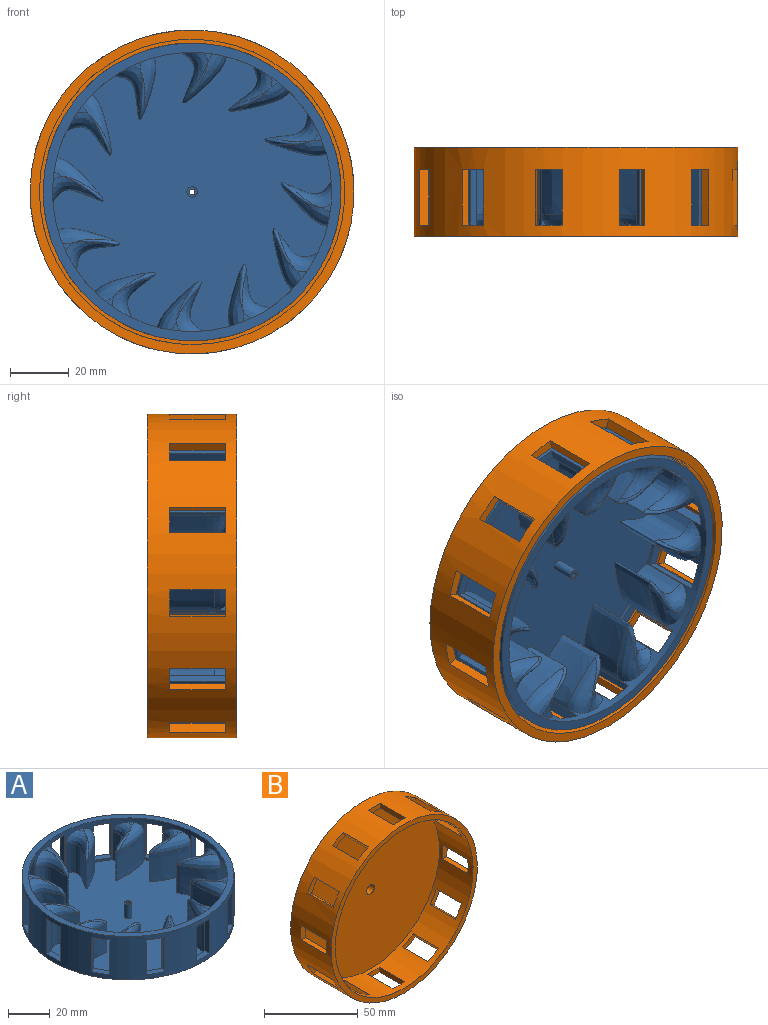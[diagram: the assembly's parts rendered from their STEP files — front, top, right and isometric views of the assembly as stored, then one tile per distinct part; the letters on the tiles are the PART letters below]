
ASSEMBLY  parts=2 mates=1
PART A: 116 faces, bbox 102.8x102.5x25.4 mm
  f0: plane 95.27x95.27mm, normal (0,0,1), area 5619.9mm2, adj f2,f54,f56,f58,f60,f62,f64,f66
  f1: cylinder r=50.8mm len=101.6mm, axis (0,0,-1), area 5873.4mm2, adj f3,f4,f5,f6,f7,f8,f9,f10
  f2: cylinder r=47.64mm len=95.27mm, axis (0,0,-1), area 1163.8mm2, adj f0,f4,f5,f6,f7,f8,f9,f10
  f3: plane 101.6x101.6mm, normal (0,0,-1), area 8104.2mm2, adj f1,f53
  f4: plane 101.6x101.6mm, normal (0,0,1), area 978.6mm2, adj f1,f2
  f5: plane 20.32x3.18mm, normal (1,0,0), area 64.6mm2, adj f1,f2,f6,f7
  f6: plane 9.15x3.39mm, normal (0,0,1), area 29mm2, adj f1,f2,f5,f8
  f7: plane 9.15x3.39mm, normal (0,0,-1), area 29mm2, adj f1,f2,f5,f8
  f8: plane 20.32x3.18mm, normal (-1,0,0), area 64.6mm2, adj f1,f2,f6,f7
  f9: plane 9.51x7.33mm, normal (0,0,1), area 29mm2, adj f1,f2,f11,f12
  f10: plane 9.51x7.33mm, normal (0,0,-1), area 29mm2, adj f1,f2,f11,f12
  f11: plane 20.32x2.75mm, normal (0.87,0.5,0), area 64.6mm2, adj f1,f2,f9,f10
  f12: plane 20.32x2.75mm, normal (-0.87,-0.5,0), area 64.6mm2, adj f1,f2,f9,f10
  f13: plane 9.51x7.32mm, normal (0,0,1), area 29mm2, adj f1,f2,f14,f16
  f14: plane 20.32x2.75mm, normal (-0.5,-0.87,0), area 64.6mm2, adj f1,f2,f13,f15
  f15: plane 9.51x7.32mm, normal (0,0,-1), area 29mm2, adj f1,f2,f14,f16
  f16: plane 20.32x2.75mm, normal (0.5,0.87,0), area 64.6mm2, adj f1,f2,f13,f15
  f17: plane 20.32x3.18mm, normal (0,1,0), area 64.6mm2, adj f1,f2,f18,f19
  f18: plane 9.15x3.39mm, normal (0,0,1), area 29mm2, adj f1,f2,f17,f20
  f19: plane 9.15x3.39mm, normal (0,0,-1), area 29mm2, adj f1,f2,f17,f20
  f20: plane 20.32x3.18mm, normal (0,-1,0), area 64.6mm2, adj f1,f2,f18,f19
  f21: plane 9.51x7.33mm, normal (0,0,1), area 29mm2, adj f1,f2,f23,f24
  f22: plane 9.51x7.33mm, normal (0,0,-1), area 29mm2, adj f1,f2,f23,f24
  f23: plane 20.32x2.75mm, normal (-0.5,0.87,0), area 64.6mm2, adj f1,f2,f21,f22
  f24: plane 20.32x2.75mm, normal (0.5,-0.87,0), area 64.6mm2, adj f1,f2,f21,f22
  f25: plane 9.51x7.32mm, normal (0,0,1), area 29mm2, adj f1,f2,f26,f28
  f26: plane 20.32x2.75mm, normal (0.87,-0.5,0), area 64.6mm2, adj f1,f2,f25,f27
  f27: plane 9.51x7.32mm, normal (0,0,-1), area 29mm2, adj f1,f2,f26,f28
  f28: plane 20.32x2.75mm, normal (-0.87,0.5,0), area 64.6mm2, adj f1,f2,f25,f27
  f29: plane 20.32x3.18mm, normal (-1,0,0), area 64.6mm2, adj f1,f2,f30,f31
  f30: plane 9.15x3.39mm, normal (0,0,1), area 29mm2, adj f1,f2,f29,f32
  f31: plane 9.15x3.39mm, normal (0,0,-1), area 29mm2, adj f1,f2,f29,f32
  f32: plane 20.32x3.18mm, normal (1,0,0), area 64.6mm2, adj f1,f2,f30,f31
  f33: plane 9.51x7.33mm, normal (0,0,1), area 29mm2, adj f1,f2,f35,f36
  f34: plane 9.51x7.33mm, normal (0,0,-1), area 29mm2, adj f1,f2,f35,f36
  f35: plane 20.32x2.75mm, normal (-0.87,-0.5,0), area 64.6mm2, adj f1,f2,f33,f34
  f36: plane 20.32x2.75mm, normal (0.87,0.5,0), area 64.6mm2, adj f1,f2,f33,f34
  f37: plane 9.51x7.32mm, normal (0,0,1), area 29mm2, adj f1,f2,f38,f40
  f38: plane 20.32x2.75mm, normal (0.5,0.87,0), area 64.6mm2, adj f1,f2,f37,f39
  f39: plane 9.51x7.32mm, normal (0,0,-1), area 29mm2, adj f1,f2,f38,f40
  f40: plane 20.32x2.75mm, normal (-0.5,-0.87,0), area 64.6mm2, adj f1,f2,f37,f39
  f41: plane 20.32x3.18mm, normal (0,-1,0), area 64.6mm2, adj f1,f2,f42,f43
  f42: plane 9.15x3.39mm, normal (0,0,1), area 29mm2, adj f1,f2,f41,f44
  f43: plane 9.15x3.39mm, normal (0,0,-1), area 29mm2, adj f1,f2,f41,f44
  f44: plane 20.32x3.18mm, normal (0,1,0), area 64.6mm2, adj f1,f2,f42,f43
  f45: plane 9.51x7.33mm, normal (0,0,1), area 29mm2, adj f1,f2,f47,f48
  f46: plane 9.51x7.33mm, normal (0,0,-1), area 29mm2, adj f1,f2,f47,f48
  f47: plane 20.32x2.75mm, normal (0.5,-0.87,0), area 64.6mm2, adj f1,f2,f45,f46
  f48: plane 20.32x2.75mm, normal (-0.5,0.87,0), area 64.6mm2, adj f1,f2,f45,f46
  f49: plane 9.51x7.32mm, normal (0,0,1), area 29mm2, adj f1,f2,f50,f52
  f50: plane 20.32x2.75mm, normal (-0.87,0.5,0), area 64.6mm2, adj f1,f2,f49,f51
  f51: plane 9.51x7.32mm, normal (0,0,-1), area 29mm2, adj f1,f2,f50,f52
  f52: plane 20.32x2.75mm, normal (0.87,-0.5,0), area 64.6mm2, adj f1,f2,f49,f51
  f53: cylinder r=0.99mm len=9.25mm, axis (0,0,1), area 57.5mm2, adj f3,f115
  f54: extruded ~21.39x16.51mm, area 688.7mm2, adj f0,f2,f78,f79,f80
  f55: plane 3.32x2.87mm, normal (0,0,1), area 4.2mm2, adj f2,f78,f80
  f56: extruded ~19.84x16.51mm, area 693.4mm2, adj f0,f2,f111,f112,f113
  f57: plane 2.98x2.71mm, normal (0,0,1), area 3.9mm2, adj f2,f111,f113
  f58: extruded ~17.34x16.94mm, area 693.4mm2, adj f0,f2,f108,f109,f110
  f59: plane 3.19x2.64mm, normal (0,0,1), area 3.9mm2, adj f2,f108,f110
  f60: extruded ~21.41x16.51mm, area 693.4mm2, adj f0,f2,f105,f106,f107
  f61: plane 3.19x2.75mm, normal (0,0,1), area 3.9mm2, adj f2,f105,f107
  f62: extruded ~19.84x16.51mm, area 693.4mm2, adj f0,f2,f102,f103,f104
  f63: plane 2.98x2.71mm, normal (0,0,1), area 3.9mm2, adj f2,f102,f104
  f64: extruded ~17.34x16.94mm, area 693.4mm2, adj f0,f2,f81,f82,f83
  f65: plane 3.19x2.64mm, normal (0,0,1), area 3.9mm2, adj f2,f81,f83
  f66: extruded ~19.84x16.51mm, area 693.4mm2, adj f0,f2,f84,f85,f86
  f67: plane 2.98x2.71mm, normal (0,0,1), area 3.9mm2, adj f2,f84,f86
  f68: extruded ~21.41x16.51mm, area 693.4mm2, adj f0,f2,f87,f88,f89
  f69: plane 3.19x2.75mm, normal (0,0,1), area 3.9mm2, adj f2,f87,f89
  f70: extruded ~17.34x16.94mm, area 693.4mm2, adj f0,f2,f90,f91,f92
  f71: plane 3.19x2.64mm, normal (0,0,1), area 3.9mm2, adj f2,f90,f92
  f72: extruded ~19.84x16.51mm, area 693.4mm2, adj f0,f2,f93,f94,f95
  f73: plane 2.98x2.71mm, normal (0,0,1), area 3.9mm2, adj f2,f93,f95
  f74: extruded ~21.41x16.51mm, area 693.4mm2, adj f0,f2,f96,f97,f98
  f75: plane 3.19x2.75mm, normal (0,0,1), area 3.9mm2, adj f2,f96,f98
  f76: extruded ~17.34x16.94mm, area 693.4mm2, adj f0,f2,f99,f100,f101
  f77: plane 3.19x2.64mm, normal (0,0,1), area 3.9mm2, adj f2,f99,f101
  f78: bspline ~21.2x15.41mm, area 80.2mm2, adj f2,f54,f55,f79
  f79: bspline ~15.38x5.94mm, area 17.3mm2, adj f54,f78,f80
  f80: bspline ~20.24x7.88mm, area 93mm2, adj f2,f54,f55,f79
  f81: bspline ~22.19x10.5mm, area 79.5mm2, adj f2,f64,f65,f82
  f82: bspline ~12.45x10.83mm, area 17.9mm2, adj f64,f81,f83
  f83: bspline ~17.85x15.35mm, area 103.8mm2, adj f2,f64,f65,f82
  f84: bspline ~19.82x11.91mm, area 79.5mm2, adj f2,f66,f67,f85
  f85: bspline ~16.09x5.08mm, area 18mm2, adj f66,f84,f86
  f86: bspline ~19.22x11.35mm, area 103.8mm2, adj f2,f66,f67,f85
  f87: bspline ~18.58x15.09mm, area 79.5mm2, adj f2,f68,f69,f88
  f88: bspline ~15.51x5.91mm, area 17.1mm2, adj f68,f87,f89
  f89: bspline ~20.23x7.78mm, area 103.8mm2, adj f2,f68,f69,f88
  f90: bspline ~17.96x15.3mm, area 104.1mm2, adj f2,f70,f71,f91
  f91: bspline ~12.45x10.83mm, area 18mm2, adj f70,f90,f92
  f92: bspline ~22.01x10.53mm, area 79.3mm2, adj f2,f70,f71,f91
  f93: bspline ~19.82x11.91mm, area 79.5mm2, adj f2,f72,f73,f94
  f94: bspline ~16.09x5.08mm, area 18mm2, adj f72,f93,f95
  f95: bspline ~19.22x11.35mm, area 103.8mm2, adj f2,f72,f73,f94
  f96: bspline ~18.58x15.09mm, area 79.5mm2, adj f2,f74,f75,f97
  f97: bspline ~15.51x5.91mm, area 17.1mm2, adj f74,f96,f98
  f98: bspline ~20.23x7.78mm, area 103.8mm2, adj f2,f74,f75,f97
  f99: bspline ~22.19x10.5mm, area 79.5mm2, adj f2,f76,f77,f100
  f100: bspline ~12.45x10.83mm, area 17.9mm2, adj f76,f99,f101
  f101: bspline ~17.85x15.35mm, area 103.8mm2, adj f2,f76,f77,f100
  f102: bspline ~19.34x11.56mm, area 104.1mm2, adj f2,f62,f63,f103
  f103: bspline ~16.09x5.08mm, area 18mm2, adj f62,f102,f104
  f104: bspline ~19.75x11.89mm, area 79.3mm2, adj f2,f62,f63,f103
  f105: bspline ~20.49x7.63mm, area 104.1mm2, adj f2,f60,f61,f106
  f106: bspline ~15.51x5.91mm, area 18mm2, adj f60,f105,f107
  f107: bspline ~18.53x15.57mm, area 79.3mm2, adj f2,f60,f61,f106
  f108: bspline ~17.96x15.3mm, area 104.1mm2, adj f2,f58,f59,f109
  f109: bspline ~12.45x10.83mm, area 18mm2, adj f58,f108,f110
  f110: bspline ~22.01x10.53mm, area 79.3mm2, adj f2,f58,f59,f109
  f111: bspline ~19.34x11.56mm, area 104.1mm2, adj f2,f56,f57,f112
  f112: bspline ~16.09x5.08mm, area 18mm2, adj f56,f111,f113
  f113: bspline ~19.75x11.89mm, area 79.3mm2, adj f2,f56,f57,f112
  f114: cylinder r=1.77mm len=7.98mm, axis (0,0,-1), area 88.5mm2, adj f0,f115
  f115: plane 3.53x3.53mm, normal (0,0,1), area 6.7mm2, adj f53,f114
PART B: 54 faces, bbox 110.5x30.5x110.5 mm
  f0: cylinder r=52.07mm len=104.14mm, axis (0,1,0), area 6192.2mm2, adj f2,f3,f5,f6,f7,f8,f9,f10
  f1: cylinder r=55.25mm len=110.49mm, axis (0,1,0), area 8462.6mm2, adj f3,f4,f5,f6,f7,f8,f9,f10
  f2: plane 104.14x104.14mm, normal (0,-1,0), area 8490.5mm2, adj f0,f53
  f3: plane 110.49x110.49mm, normal (0,-1,0), area 1070.4mm2, adj f0,f1
  f4: plane 110.49x110.49mm, normal (0,1,0), area 9560.9mm2, adj f1,f53
  f5: plane 9.6x7.41mm, normal (0,-1,0), area 29.4mm2, adj f0,f1,f7,f8
  f6: plane 9.6x7.41mm, normal (0,1,0), area 29.4mm2, adj f0,f1,f7,f8
  f7: plane 19.05x2.75mm, normal (0.86,0,-0.5), area 60.7mm2, adj f0,f1,f5,f6
  f8: plane 19.05x2.75mm, normal (-0.86,0,0.5), area 60.7mm2, adj f0,f1,f5,f6
  f9: plane 9.27x3.4mm, normal (0,-1,0), area 29.4mm2, adj f0,f1,f10,f12
  f10: plane 19.05x3.19mm, normal (1,0,0), area 60.7mm2, adj f0,f1,f9,f11
  f11: plane 9.27x3.4mm, normal (0,1,0), area 29.4mm2, adj f0,f1,f10,f12
  f12: plane 19.05x3.19mm, normal (-1,0,0), area 60.7mm2, adj f0,f1,f9,f11
  f13: plane 19.05x2.77mm, normal (-0.87,0,-0.5), area 60.7mm2, adj f0,f1,f14,f15
  f14: plane 9.61x7.36mm, normal (0,-1,0), area 29.4mm2, adj f0,f1,f13,f16
  f15: plane 9.61x7.36mm, normal (0,1,0), area 29.4mm2, adj f0,f1,f13,f16
  f16: plane 19.05x2.77mm, normal (0.87,0,0.5), area 60.7mm2, adj f0,f1,f14,f15
  f17: plane 9.6x7.41mm, normal (0,-1,0), area 29.4mm2, adj f0,f1,f19,f20
  f18: plane 9.6x7.41mm, normal (0,1,0), area 29.4mm2, adj f0,f1,f19,f20
  f19: plane 19.05x2.75mm, normal (-0.5,0,-0.86), area 60.7mm2, adj f0,f1,f17,f18
  f20: plane 19.05x2.75mm, normal (0.5,0,0.86), area 60.7mm2, adj f0,f1,f17,f18
  f21: plane 9.27x3.4mm, normal (0,-1,0), area 29.4mm2, adj f0,f1,f22,f24
  f22: plane 19.05x3.19mm, normal (0,0,1), area 60.7mm2, adj f0,f1,f21,f23
  f23: plane 9.27x3.4mm, normal (0,1,0), area 29.4mm2, adj f0,f1,f22,f24
  f24: plane 19.05x3.19mm, normal (0,0,-1), area 60.7mm2, adj f0,f1,f21,f23
  f25: plane 19.05x2.77mm, normal (0.5,0,-0.87), area 60.7mm2, adj f0,f1,f26,f27
  f26: plane 9.61x7.36mm, normal (0,-1,0), area 29.4mm2, adj f0,f1,f25,f28
  f27: plane 9.61x7.36mm, normal (0,1,0), area 29.4mm2, adj f0,f1,f25,f28
  f28: plane 19.05x2.77mm, normal (-0.5,0,0.87), area 60.7mm2, adj f0,f1,f26,f27
  f29: plane 9.6x7.41mm, normal (0,-1,0), area 29.4mm2, adj f0,f1,f31,f32
  f30: plane 9.6x7.41mm, normal (0,1,0), area 29.4mm2, adj f0,f1,f31,f32
  f31: plane 19.05x2.75mm, normal (0.86,0,-0.5), area 60.7mm2, adj f0,f1,f29,f30
  f32: plane 19.05x2.75mm, normal (-0.86,0,0.5), area 60.7mm2, adj f0,f1,f29,f30
  f33: plane 9.27x3.4mm, normal (0,-1,0), area 29.4mm2, adj f0,f1,f34,f36
  f34: plane 19.05x3.19mm, normal (-1,0,0), area 60.7mm2, adj f0,f1,f33,f35
  f35: plane 9.27x3.4mm, normal (0,1,0), area 29.4mm2, adj f0,f1,f34,f36
  f36: plane 19.05x3.19mm, normal (1,0,0), area 60.7mm2, adj f0,f1,f33,f35
  f37: plane 19.05x2.77mm, normal (0.87,0,0.5), area 60.7mm2, adj f0,f1,f38,f39
  f38: plane 9.61x7.36mm, normal (0,-1,0), area 29.4mm2, adj f0,f1,f37,f40
  f39: plane 9.61x7.36mm, normal (0,1,0), area 29.4mm2, adj f0,f1,f37,f40
  f40: plane 19.05x2.77mm, normal (-0.87,0,-0.5), area 60.7mm2, adj f0,f1,f38,f39
  f41: plane 9.6x7.41mm, normal (0,-1,0), area 29.4mm2, adj f0,f1,f43,f44
  f42: plane 9.6x7.41mm, normal (0,1,0), area 29.4mm2, adj f0,f1,f43,f44
  f43: plane 19.05x2.75mm, normal (0.5,0,0.86), area 60.7mm2, adj f0,f1,f41,f42
  f44: plane 19.05x2.75mm, normal (-0.5,0,-0.86), area 60.7mm2, adj f0,f1,f41,f42
  f45: plane 9.27x3.4mm, normal (0,-1,0), area 29.4mm2, adj f0,f1,f46,f48
  f46: plane 19.05x3.19mm, normal (0,0,-1), area 60.7mm2, adj f0,f1,f45,f47
  f47: plane 9.27x3.4mm, normal (0,1,0), area 29.4mm2, adj f0,f1,f46,f48
  f48: plane 19.05x3.19mm, normal (0,0,1), area 60.7mm2, adj f0,f1,f45,f47
  f49: plane 9.61x7.36mm, normal (0,-1,0), area 29.4mm2, adj f0,f1,f51,f52
  f50: plane 9.61x7.36mm, normal (0,1,0), area 29.4mm2, adj f0,f1,f51,f52
  f51: plane 19.05x2.77mm, normal (-0.5,0,0.87), area 60.7mm2, adj f0,f1,f49,f50
  f52: plane 19.05x2.77mm, normal (0.5,0,-0.87), area 60.7mm2, adj f0,f1,f49,f50
  f53: cylinder r=2.95mm len=5.89mm, axis (0,-1,0), area 94mm2, adj f2,f4
PLACE A rot(axis=(0.51,-0.61,0.61),125.9deg) t=(-96.45,11.11,59.47)mm
PLACE B rot(axis=(0,-1,0),100deg) t=(-96.45,16.19,59.47)mm
MATE fastened B.f0 <-> A.f1  axis (0,-1,0) through (-96.45,11.11,59.47)mm
